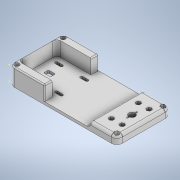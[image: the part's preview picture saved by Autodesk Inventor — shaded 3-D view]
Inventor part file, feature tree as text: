
AUTODESK INVENTOR PART (.ipt)
format: ipt  version: 2021 (Build 250183000, 183)  size: 785,920 bytes
history: native  units: mm
features: extrude x13, sketch x12, fillet x6, hole x2
ambient origin geometry x8: Origin, YZ Plane, XZ Plane, XY Plane, X Axis, Y Axis, Z Axis, Center Point
bodies: Solid1 (feature_tree)
feature tree (33):
  extrude  "Extrusion1"  Depth=2.0mm
  fillet  "Fillet3"  Radius=5.0mm
  hole  "Hole2"  [1 undecoded]
  hole  "Otwór3"  [1 undecoded]
  extrude  "Wyciągnięcie proste7"  Depth=2.0mm
  extrude  "Wyciągnięcie proste8"  Depth=2.0mm
  extrude  "Wyciągnięcie proste9"  Depth=2.0mm
  extrude  "Wyciągnięcie proste10"  TaperAngle=0.0deg  [1 undecoded]
  fillet  "Zaokrąglenie4"  Radius=7.0mm
  fillet  "Zaokrąglenie5"  Radius=7.0mm
  fillet  "Zaokrąglenie6"  Radius=72.0mm
  extrude  "Wyciągnięcie proste13"  Depth=2.0mm
  extrude  "Wyciągnięcie proste14"  Depth=2.0mm
  extrude  "Wyciągnięcie proste15"  Depth=10.0mm TaperAngle=0.0deg
  extrude  "Wyciągnięcie proste16"  Depth=10.0mm TaperAngle=0.0deg
  sketch  "Szkic65"
  extrude  "Wyciągnięcie proste19"  Depth=2.0mm TaperAngle=0.0deg
  extrude  "Wyciągnięcie proste20"  Depth=2.0mm
  extrude  "Wyciągnięcie proste21"  Depth=2.0mm
  extrude  "Wyciągnięcie proste22"  Depth=2.0mm
  fillet  "Zaokrąglenie10"  Radius=5.0mm
  sketch  "Szkic73"
  fillet  "Zaokrąglenie11"  Radius=3.0mm
  sketch  "Szkic74"
  sketch  "Szkic75"
  sketch  "Sketch2"  dims[d0=200.0mm d1=100.0mm d2=5.0mm d3=0.0mm d31=10.0mm d32=200.0mm d33=100.0mm d34=7.0mm d35=7.0mm d36=7.0mm d37=7.0mm d38=5.0mm d39=6.0mm d40=4.0mm d41=2.0mm d42=90.0deg d43=18.0mm d44=0.0mm d82=200.0mm d83=100.0mm d84=100.0mm d85=50.0mm d86=50.0mm d87=38.45mm d88=25.0mm d89=7.5mm d90=3.75mm d91=1.0mm d92=180.0deg d93=12.0mm d94=2.0mm d95=2.0mm d96=10.0mm d97=1.0mm d98=20.0mm d99=50.0mm d100=5.0mm d101=6.0mm d102=4.0mm d103=2.0mm d104=90.0deg d105=8.0mm d106=20.594885mm d107=200.0mm d108=100.0mm d109=100.0mm d110=50.0mm d111=50.0mm d112=38.45mm d113=25.0mm d114=7.5mm d115=3.75mm d116=1.0mm d117=180.0deg d118=12.0mm d119=2.0mm d120=2.0mm d121=10.0mm d122=1.0mm d123=20.0mm d124=50.0mm d125=0.0mm d126=0.0mm d140=7.0mm d141=7.0mm d142=72.0mm d143=14.0mm d144=15.0mm d145=10.0mm d146=0.0mm d147=10.0mm d148=0.0mm d151=6.0mm d152=0.0mm d153=5.0mm d154=2.0mm d155=6.0mm d172=5.0mm d174=3.0mm d176=12.5mm d177=12.5mm d178=12.5mm d179=0.0mm d180=0.0mm d182=19.65mm d184=15.5mm d185=3.0mm d186=3.0mm d187=3.5mm d188=6.0mm d189=12.5mm d190=6.0mm d191=5.0mm d192=3.0mm d193=12.5mm d194=12.5mm d195=12.5mm d196=19.65mm d204=0.0mm d205=0.0mm d223=6.0mm d224=0.0mm d233=0.0mm d234=0.0mm d269=1.575mm d272=4.575mm d274=4.575mm d275=4.575mm d276=4.575mm d277=0.0mm d278=0.0mm d279=1.575mm d281=4.575mm d282=4.575mm d283=4.575mm d284=10.0mm d285=10.0mm d286=10.0mm d287=10.0mm d288=10.0mm d289=5.0mm d290=0.0mm d291=1.575mm d292=4.575mm d293=4.575mm d294=4.575mm d295=10.0mm d296=10.0mm d297=10.0mm d298=10.0mm d299=10.0mm d300=0.2mm d301=0.2mm d302=0.2mm d303=0.2mm d305=0.2mm d306=27.0mm d307=0.0mm d308=8.5mm d309=8.5mm d310=27.0mm d311=0.0mm d312=2.0mm d313=2.0mm d65=0.5mm d66=0.872665mm d67=0.5mm d68=0.872665mm d80=0.5mm d81=0.872665mm d127=0.5mm d128=0.872665mm d129=0.5mm d130=0.872665mm d131=0.5mm d132=0.872665mm]
  sketch  "Szkic17"
  sketch  "Szkic20"
  sketch  "Szkic43"
  sketch  "Szkic44"
  sketch  "Szkic70"
  sketch  "Szkic71"
  sketch  "Szkic72"
note: 3 required parameter values undecoded (feature->parameter linkage not recoverable at this tier; creation-order binding heuristic only, values carry confidence <= 0.55)
